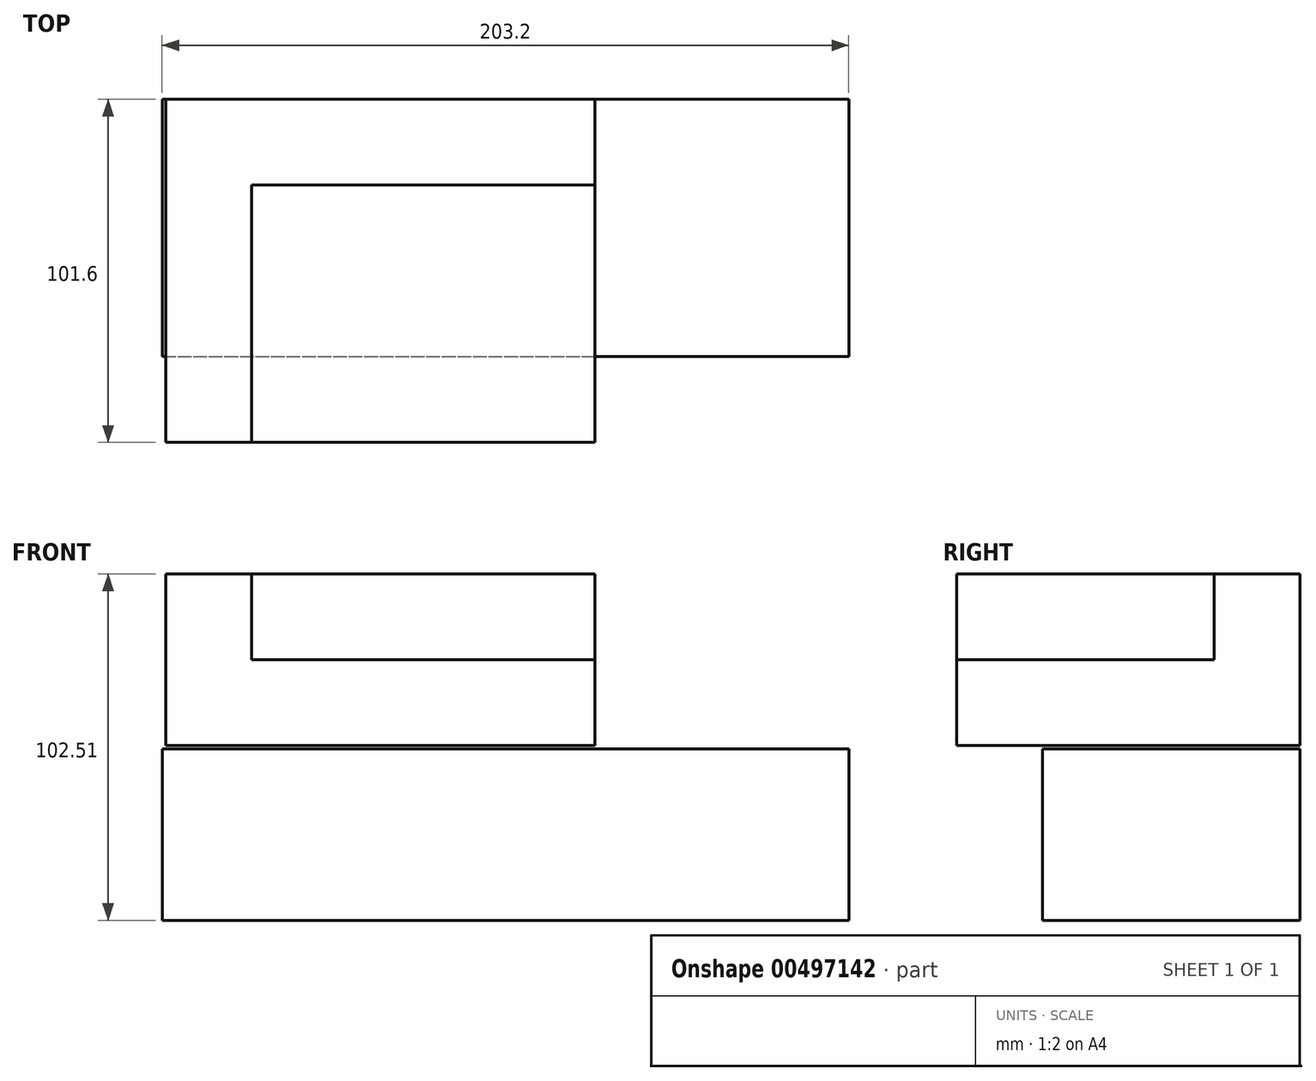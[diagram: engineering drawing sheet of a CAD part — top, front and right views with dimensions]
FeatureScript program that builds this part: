
annotation { "Feature Type Name" : "Feature", "Feature Type Description" : "" }
export const myFeature = defineFeature(function(context is Context, id is Id, definition is map)
    precondition{}
    {
        {
            var Q0;
            Q0=qCreatedBy(makeId("Front.planeOp"),FACE);
            var sketch = newSketch(context, id + "F0", { "sketchPlane" : qUnion([Q0])});
            skLineSegment(sketch, "E0.bottom", {"start": v(-94.79, -51.71) * mm, "end": v(108.41, -51.71) * mm});
            skLineSegment(sketch, "E0.top", {"start": v(-94.79, -0.91) * mm, "end": v(108.41, -0.91) * mm});
            skLineSegment(sketch, "E0.left", {"start": v(-94.79, -51.71) * mm, "end": v(-94.79, -0.91) * mm});
            skLineSegment(sketch, "E0.right", {"start": v(108.41, -51.71) * mm, "end": v(108.41, -0.91) * mm});
            skSolve(sketch);
        }
        {
            var Q0;
            Q0 = qSketchRegion(id + "F0", true);
            extrude(context, id + "F1", {"entities" : qUnion([Q0]), "depth" : 76.2 * mm});
        }
        {
            var Q0;
            Q0=qCreatedBy(makeId("Top.planeOp"),FACE);
            var sketch = newSketch(context, id + "F2", { "sketchPlane" : qUnion([Q0])});
            skLineSegment(sketch, "E1.bottom", {"start": v(-93.7, 0) * mm, "end": v(33.3, 0) * mm});
            skLineSegment(sketch, "E1.top", {"start": v(-93.7, -101.6) * mm, "end": v(33.3, -101.6) * mm});
            skLineSegment(sketch, "E1.left", {"start": v(-93.7, 0) * mm, "end": v(-93.7, -101.6) * mm});
            skLineSegment(sketch, "E1.right", {"start": v(33.3, 0) * mm, "end": v(33.3, -101.6) * mm});
            skSolve(sketch);
        }
        {
            var Q0;
            Q0 = qSketchRegion(id + "F2", true);
            extrude(context, id + "F3", {"entities" : qUnion([Q0]), "depth" : 25.4 * mm});
        }
        {
            var Q0;
            Q0=makeQuery(id+"F3.opExtrude","CAP_FACE",FACE,{"disambiguationData":[OSD([sQuery(id+"F2.wireOp",EDGE,"E1.bottom"),sQuery(id+"F2.wireOp",EDGE,"E1.top"),sQuery(id+"F2.wireOp",EDGE,"E1.left"),sQuery(id+"F2.wireOp",EDGE,"E1.right")])],"isStart":false});
            var sketch = newSketch(context, id + "F4", { "sketchPlane" : qUnion([Q0])});
            skLineSegment(sketch, "E2.bottom", {"start": v(-93.7, 0) * mm, "end": v(-68.3, 0) * mm});
            skLineSegment(sketch, "E2.top", {"start": v(-93.7, -101.6) * mm, "end": v(-68.3, -101.6) * mm});
            skLineSegment(sketch, "E2.left", {"start": v(-93.7, 0) * mm, "end": v(-93.7, -101.6) * mm});
            skLineSegment(sketch, "E2.right", {"start": v(-68.3, 0) * mm, "end": v(-68.3, -101.6) * mm});
            skLineSegment(sketch, "E3.bottom", {"start": v(-93.7, 0) * mm, "end": v(33.3, 0) * mm});
            skLineSegment(sketch, "E3.top", {"start": v(-93.7, -25.4) * mm, "end": v(33.3, -25.4) * mm});
            skLineSegment(sketch, "E3.left", {"start": v(-93.7, 0) * mm, "end": v(-93.7, -25.4) * mm});
            skLineSegment(sketch, "E3.right", {"start": v(33.3, 0) * mm, "end": v(33.3, -25.4) * mm});
            skSolve(sketch);
        }
        {
            var Q0;
            Q0 = qSketchRegion(id + "F4", true);
            extrude(context, id + "F5", {"entities" : qUnion([Q0]), "operationType" : NewBodyOperationType.ADD, "depth" : 25.4 * mm});
        }
    });
